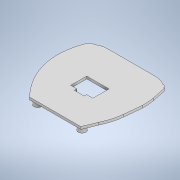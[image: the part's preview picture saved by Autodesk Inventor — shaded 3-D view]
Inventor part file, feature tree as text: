
AUTODESK INVENTOR PART (.ipt)
format: ipt  version: 2022 (Build 260153000, 153)  size: 290,304 bytes
history: native  units: mm
features: extrude x4, other x2, sketch x1
ambient origin geometry x8: Origin, YZ Plane, XZ Plane, XY Plane, X Axis, Y Axis, Z Axis, Center Point
bodies: Body1 (feature_tree)
feature tree (7):
  other  "솔리드2"
  other  "작업 평면16"
  sketch  "스케치46"
  extrude  "돌출51"  Depth=54.41318mm
  extrude  "돌출53"  Depth=2.0mm
  extrude  "돌출54"  Depth=3.0mm TaperAngle=0.0deg
  extrude  "돌출55"  Depth=7.0mm TaperAngle=0.0deg
